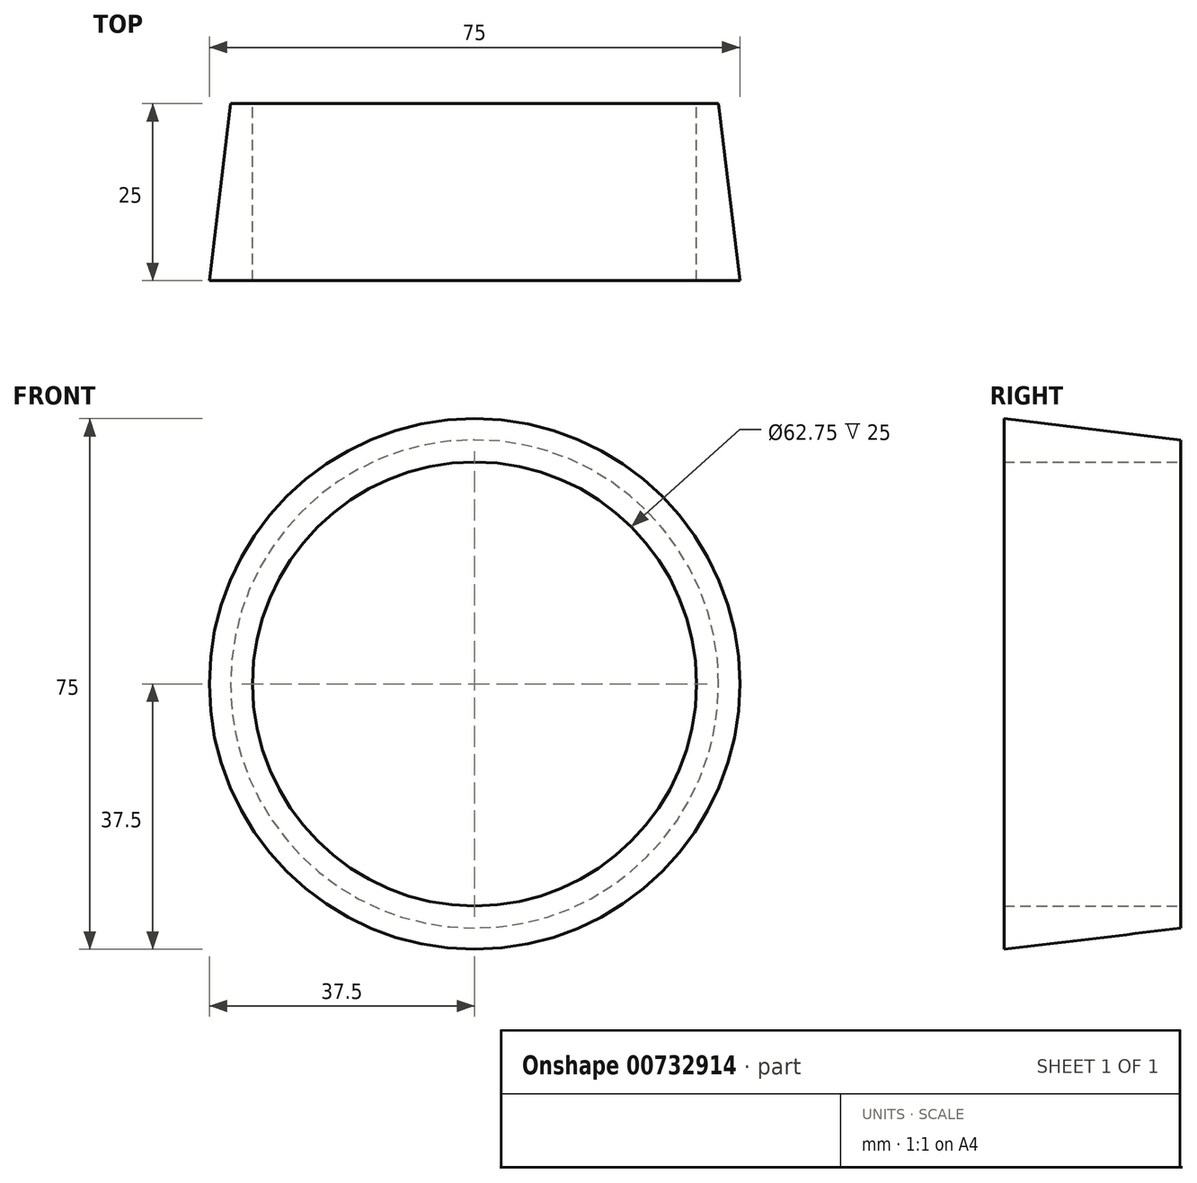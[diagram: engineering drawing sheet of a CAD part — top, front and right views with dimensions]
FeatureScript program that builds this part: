
annotation { "Feature Type Name" : "Feature", "Feature Type Description" : "" }
export const myFeature = defineFeature(function(context is Context, id is Id, definition is map)
    precondition{}
    {
        {
            var Q0;
            Q0=qCreatedBy(makeId("Front.planeOp"),FACE);
            var sketch = newSketch(context, id + "F0", { "sketchPlane" : qUnion([Q0])});
            skCircle(sketch, "E0", {"center": v(0, 0) * mm, "radius": 31.38 * mm});
            skCircle(sketch, "E1", {"center": v(0, 0) * mm, "radius": 37.5 * mm});
            skSolve(sketch);
        }
        {
            var Q0;
            Q0=makeQuery(id+"F0.imprint","IMPRINT",FACE,{"disambiguationData":[TD([[makeQuery(id+"F0.imprint","IMPRINT",EDGE,{"derivedFrom":sQuery(id+"F0.wireOp",EDGE,"E0")}),-1.0]])]});
            extrude(context, id + "F1", {"entities" : qUnion([Q0]), "depth" : 25 * mm, "offsetDistance" : 25 * mm});
        }
        {
            var Q0;
            Q0=makeQuery(id+"F1.opExtrude","CAP_EDGE",EDGE,{"disambiguationData":[OSD([sQuery(id+"F0.wireOp",EDGE,"E1")])],"isStart":true});
            chamfer(context, id + "F2", {"entities" : qUnion([Q0]), "chamferType" : ChamferType.TWO_OFFSETS, "width1" : 25 * mm, "oppositeDirection" : false, "width2" : 3 * mm, "tangentPropagation" : true});
        }
    });
